# Revit family: Pilona Telescopica Automatica
name_source: partatom
category: Furniture
units: mm (PartAtom-declared; Revit-internal decimal feet)

## family parameters
Always vertical = Yes
Cut with Voids When Loaded = No
Room Calculation Point = No
Shared = No
Work Plane-Based = No

## types (6) — shared parameters
A = 0.22 m
A1 = 0.2 m
B = 0.274 m
C = 0.34 m
Fabricante = BENITO URBAN SL
Ficha técnica = https://www.benito.com
Material = Acero inoxidable
Type Comments = Tiene un consumo de 600W y una potencia Motor 300 W (3000r.p.m) con grado de Protección IP 67. El tiempo de subida / bajada es de 4seg
URL Producto = https://www.benito.com
a = 0.02 m
zero-valued in all types: Default Elevation

## per-type parameters (varying)
| type | D | Description | Espesor | H | H1 | Referencia |
| Pilona Automatica-H6004-220mm | 0.6 m | Pilona automática fabricada con émbolo de acero inoxidable AISI-304 satinado de Ø220 x 600 mm de altura | 0.004 m | 1.47 m | 0.87 m | H6004 |
| Pilona Automatica-H6008-220mm | 0.6 m | Pilona automática fabricada con émbolo de acero inoxidable AISI-304 satinado de Ø220 x 600 mm de altura | 0.008 m | 1.47 m | 0.87 m | H6008 |
| Pilona Automatica-H60013-220mm | 0.6 m | Pilona automática fabricada con émbolo de acero inoxidable AISI-304 satinado de Ø220 x 600 mm de altura | 0.013 m | 1.66 m | 1.06 m | H60013 |
| Pilona Automatica-H7504-220mm | 0.75 m | Pilona automática fabricada con émbolo de acero inoxidable AISI-304 satinado de Ø220 x 750 mm de altura | 0.004 m | 1.81 m | 1.06 m | H7504 |
| Pilona Automatica-H7508-220mm | 0.75 m | Pilona automática fabricada con émbolo de acero inoxidable AISI-304 satinado de Ø220 x 750 mm de altura | 0.008 m | 1.81 m | 1.06 m | H7508 |
| Pilona Automatica-H75013-220mm | 0.75 m | Pilona automática fabricada con émbolo de acero inoxidable AISI-304 satinado de Ø220 x 750 mm de altura | 0.008 m | 1.96 m | 1.21 m | H75013 |

## geometry (parser evidence)
native form markers: Blend x2, Sweep x3
no freeform markers — native parametric forms only
